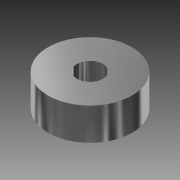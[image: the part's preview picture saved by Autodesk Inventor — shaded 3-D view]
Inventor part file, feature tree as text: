
AUTODESK INVENTOR PART (.ipt)
format: ipt  version: 2013 (Build 170138000, 138)  size: 93,184 bytes
history: native  units: mm
features: extrude x1, sketch x1
ambient origin geometry x8: Origin, YZ Plane, XZ Plane, XY Plane, X Axis, Y Axis, Z Axis, Center Point
bodies: Solid1 (feature_tree)
feature tree (2):
  extrude  "Extrusion1"  Depth=4.0mm
  sketch  "Sketch1"  dims[d0=13.0mm d2=4.0mm d3=5.0mm d4=0.0mm]
